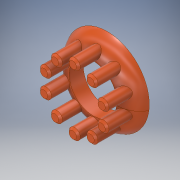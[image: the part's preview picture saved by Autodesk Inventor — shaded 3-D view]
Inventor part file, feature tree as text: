
AUTODESK INVENTOR PART (.ipt)
format: ipt  version: 2019.2 (Build 232265000, 265)  size: 1,290,752 bytes
history: native  units: mm
features: other x4, sketch x2, extrude x2, plane x1, revolve x1, chamfer x1, pattern_circular x1
ambient origin geometry x8: Origin, YZ Plane, XZ Plane, XY Plane, X Axis, Y Axis, Z Axis, Center Point
bodies: Solid1 (feature_tree)
feature tree (12):
  other  "Orangatang_Kegel_Flat_Face_Adapter"
  other  "Work Axis1"
  other  "Work Point1"
  plane  "Work Plane1"
  revolve  "Revolution1"  [1 undecoded]
  sketch  "Sketch2"  dims[d2=15.85mm d3=10.0mm d4=0.0mm d5=18.0mm d6=0.0mm d7=1.0mm d8=2.0mm d9=45.0deg d10=100.0mm d11=360.0deg]
  extrude  "Extrusion1"  Depth=10.0mm TaperAngle=0.0deg
  extrude  "Extrusion2"  Depth=10.0mm TaperAngle=0.0deg
  chamfer  "Chamfer1"  Distance=1.0mm Angle=45.0deg
  pattern_circular  "Circular Pattern1"  Count=10 Angle=360.0deg
  sketch  "Sketch1"  dims[d0=90.0deg d1=5.8mm]
  other  "MeshFeature1"
note: 1 required parameter value undecoded (feature->parameter linkage not recoverable at this tier; creation-order binding heuristic only, values carry confidence <= 0.55)
